# Revit family: QF_ELECTROLUXPROFESSIONAL_589477_MCKDFADDPO
name_source: partatom
category: Specialty Equipment
units: mm (PartAtom-declared; Revit-internal decimal feet)

## family parameters
Always vertical = Yes
Cut with Voids When Loaded = No
Enable Cutting in Views = No
Maintain Annotation Orientation = No
Part Type = Normal
Room Calculation Point = No
Round Connector Dimension = Use Diameter
Shared = No
Work Plane-Based = No

## types (1)
- QF_ELECTROLUXPROFESSIONAL_589477_MCKDFADDPO
    Accessory = No
    Cold Water Connection Height = 0 mm  [stored 0 ft]
    Cold Water Maximum Pressure = 0.00 psi
    Cold Water Minimum Pressure = 0.00 psi
    Cold Water Size = 1"
    Default Elevation = 0 mm  [stored 0 ft]
    Depth Actual = 900 mm  [stored 2.95276 ft]
    Description = GAS PASTA COOKER, 1X24,5L, 1-SIDE, 400X900X800H
    Direct Waste Size = 1"
    Gas Connection Height = 0 mm  [stored 0 ft]
    Gas Input Pressure = 1.2
    Gas KW = 11.5
    Gas Size = 1"
    HP = 0 HP
    Height Actual = 800 mm  [stored 2.62467 ft]
    Indirect Waste Connection Height = 0 mm  [stored 0 ft]
    Indirect Waste Size = 1"
    Length Actual = 400 mm  [stored 1.31234 ft]
    Manufacturer = Electrolux Professional
    Model = MCKDFADDPO
    URL = http://www.electroluxprofessional.com
    URL Manufacturer = http://www.electroluxprofessional.com
    Watts = 0 W
    Weight = 73.00 kg
    Weight in Pounds = 160.9

note: source unit labels omitted for Gas Input Pressure — the stored unit's dimension contradicts the parameter name (converter mislabeling)

note: [stored X ft] marks values corroborated as IEEE doubles in the binary element streams (Revit-internal decimal feet)

## geometry (parser evidence)
native form markers: Blend x6, Sweep x9
no freeform markers — native parametric forms only
